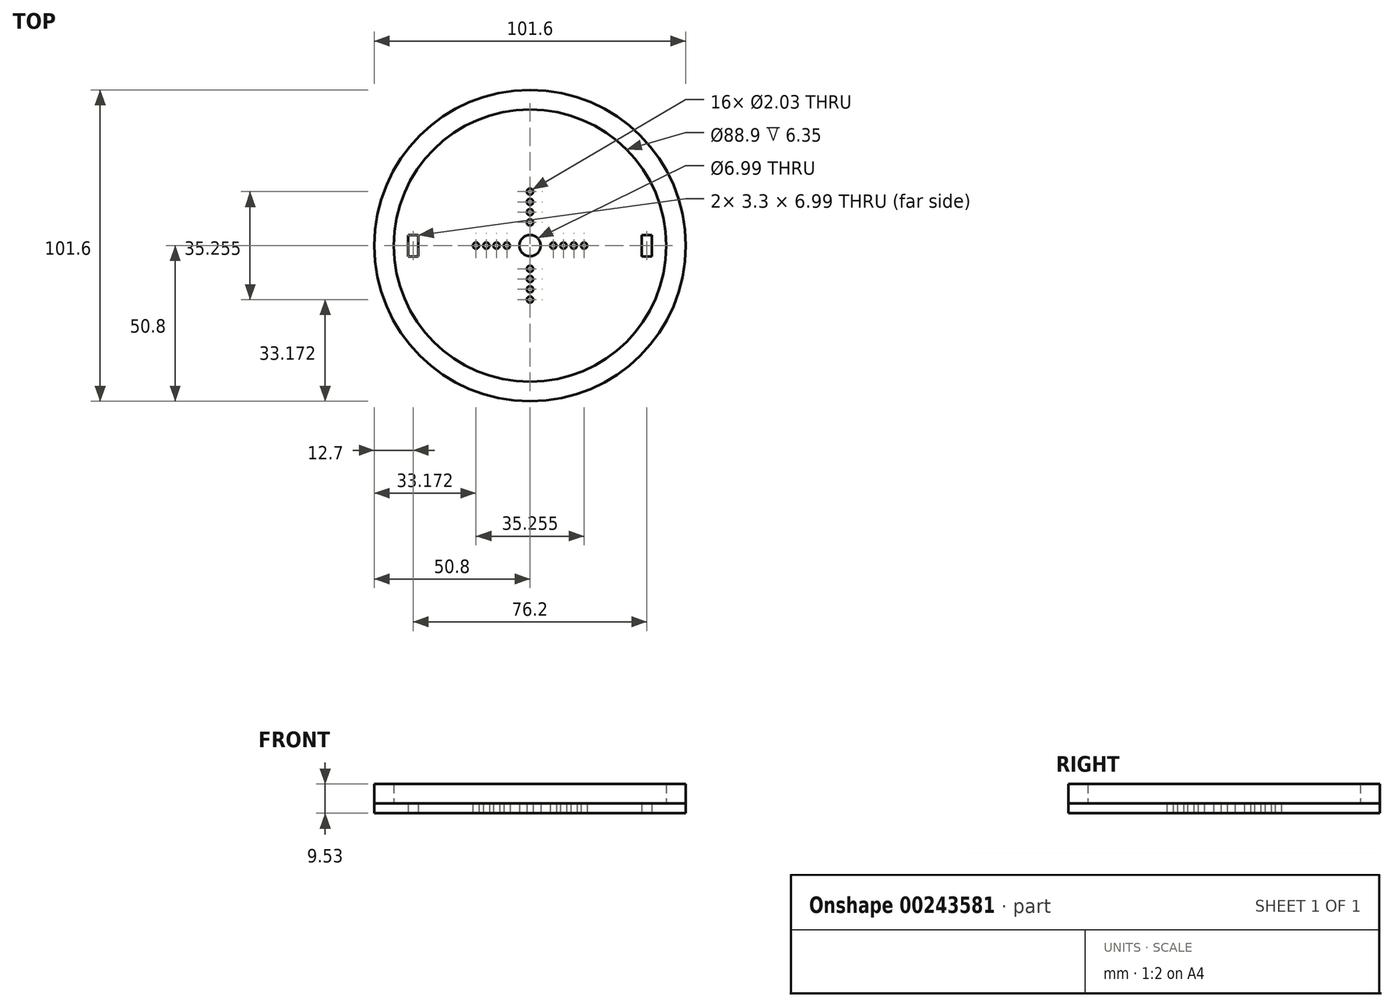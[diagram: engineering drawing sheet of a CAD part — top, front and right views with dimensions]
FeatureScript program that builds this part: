
annotation { "Feature Type Name" : "Feature", "Feature Type Description" : "" }
export const myFeature = defineFeature(function(context is Context, id is Id, definition is map)
    precondition{}
    {
        {
            var Q0;
            Q0=qCreatedBy(makeId("Top.planeOp"),FACE);
            var sketch = newSketch(context, id + "F0", { "sketchPlane" : qUnion([Q0])});
            skCircle(sketch, "E0", {"center": v(0, 0) * mm, "radius": 50.8 * mm});
            skLineSegment(sketch, "E1.bottom", {"start": v(39.75, -3.5) * mm, "end": v(36.45, -3.5) * mm});
            skLineSegment(sketch, "E1.top", {"start": v(39.75, 3.5) * mm, "end": v(36.45, 3.5) * mm});
            skLineSegment(sketch, "E1.left", {"start": v(39.75, -3.5) * mm, "end": v(39.75, 3.5) * mm});
            skLineSegment(sketch, "E1.right", {"start": v(36.45, -3.5) * mm, "end": v(36.45, 3.5) * mm});
            skPoint(sketch, "E1.middle", {"position": v(38.1, 0) * mm});
            skLineSegment(sketch, "E2.MirrorCS", {"start": v(-39.75, -3.5) * mm, "end": v(-36.45, -3.5) * mm});
            skLineSegment(sketch, "E3.MirrorCS", {"start": v(-39.75, -3.5) * mm, "end": v(-39.75, 3.5) * mm});
            skLineSegment(sketch, "E4.MirrorCS", {"start": v(-39.75, 3.5) * mm, "end": v(-36.45, 3.5) * mm});
            skLineSegment(sketch, "E5.MirrorCS", {"start": v(-36.45, -3.5) * mm, "end": v(-36.45, 3.5) * mm});
            skCircle(sketch, "E6", {"center": v(0, 0) * mm, "radius": 3.5 * mm});
            skCircle(sketch, "E7", {"center": v(-7.57, 0) * mm, "radius": 0.86 * mm, "construction": true});
            skCircle(sketch, "E8", {"center": v(-10.92, 0) * mm, "radius": 0.86 * mm, "construction": true});
            skCircle(sketch, "E9", {"center": v(-14.27, 0) * mm, "radius": 0.86 * mm, "construction": true});
            skCircle(sketch, "E10", {"center": v(-17.63, 0) * mm, "radius": 0.86 * mm, "construction": true});
            skCircle(sketch, "E11", {"center": v(-7.57, 0) * mm, "radius": 1.02 * mm});
            skCircle(sketch, "E12", {"center": v(-10.92, 0) * mm, "radius": 1.02 * mm});
            skCircle(sketch, "E13", {"center": v(-14.27, 0) * mm, "radius": 1.02 * mm});
            skCircle(sketch, "E14", {"center": v(-17.63, 0) * mm, "radius": 1.02 * mm});
            skCircle(sketch, "E15.1.0", {"center": v(0, 7.57) * mm, "radius": 1.02 * mm});
            skCircle(sketch, "E15.1.1", {"center": v(0, 10.92) * mm, "radius": 1.02 * mm});
            skCircle(sketch, "E15.1.2", {"center": v(0, 14.27) * mm, "radius": 1.02 * mm});
            skCircle(sketch, "E15.1.3", {"center": v(0, 17.63) * mm, "radius": 1.02 * mm});
            skCircle(sketch, "E15.2.0", {"center": v(7.57, 0) * mm, "radius": 1.02 * mm});
            skCircle(sketch, "E15.2.1", {"center": v(10.92, 0) * mm, "radius": 1.02 * mm});
            skCircle(sketch, "E15.2.2", {"center": v(14.27, 0) * mm, "radius": 1.02 * mm});
            skCircle(sketch, "E15.2.3", {"center": v(17.63, 0) * mm, "radius": 1.02 * mm});
            skCircle(sketch, "E15.3.0", {"center": v(0, -7.57) * mm, "radius": 1.02 * mm});
            skCircle(sketch, "E15.3.1", {"center": v(0, -10.92) * mm, "radius": 1.02 * mm});
            skCircle(sketch, "E15.3.2", {"center": v(0, -14.27) * mm, "radius": 1.02 * mm});
            skCircle(sketch, "E15.3.3", {"center": v(0, -17.63) * mm, "radius": 1.02 * mm});
            skLineSegment(sketch, "E15.anchor1", {"start": v(0, 0) * mm, "end": v(-7.57, 0) * mm, "construction": true});
            skLineSegment(sketch, "E15.anchor2", {"start": v(0, 0) * mm, "end": v(0, -7.57) * mm, "construction": true});
            skSolve(sketch);
        }
        {
            var Q0;
            Q0 = qSketchRegion(id + "F0", true);
            extrude(context, id + "F1", {"entities" : qUnion([Q0]), "depth" : 3.17 * mm});
        }
        {
            var Q0;
            Q0=makeQuery(id+"F1.opExtrude","CAP_FACE",FACE,{"disambiguationData":[OSD([sQuery(id+"F0.wireOp",EDGE,"E0")])],"isStart":false});
            var sketch = newSketch(context, id + "F2", { "sketchPlane" : qUnion([Q0])});
            skCircle(sketch, "E16.0", {"center": v(0, 0) * mm, "radius": 50.8 * mm});
            skCircle(sketch, "E17.0", {"center": v(0, 0) * mm, "radius": 44.45 * mm});
            skSolve(sketch);
        }
        {
            var Q0;
            Q0 = qSketchRegion(id + "F2", true);
            extrude(context, id + "F3", {"entities" : qUnion([Q0]), "depth" : 6.35 * mm});
        }
    });
